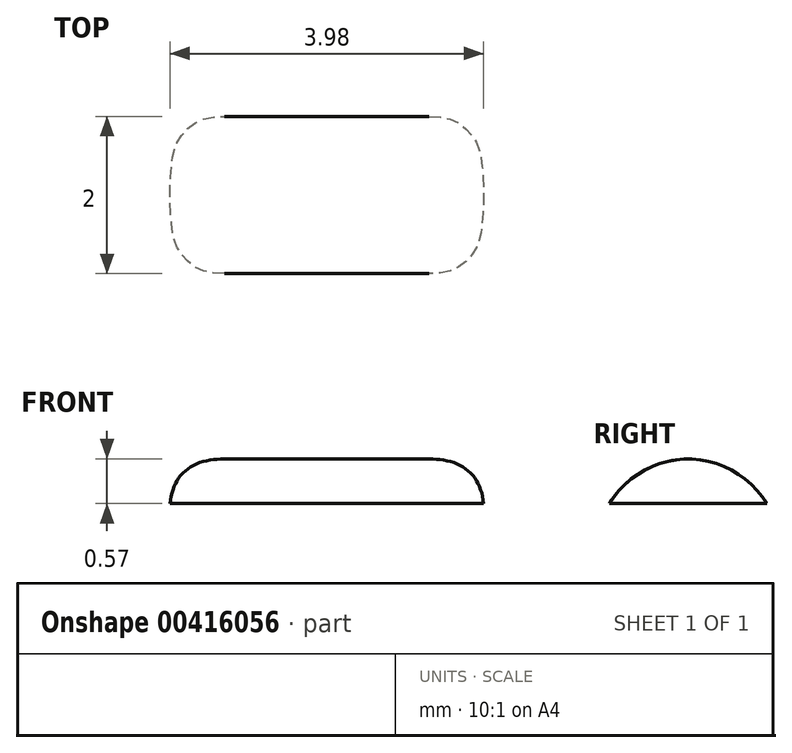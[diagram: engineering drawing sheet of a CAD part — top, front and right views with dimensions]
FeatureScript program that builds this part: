
annotation { "Feature Type Name" : "Feature", "Feature Type Description" : "" }
export const myFeature = defineFeature(function(context is Context, id is Id, definition is map)
    precondition{}
    {
        {
            var Q0;
            Q0=qCreatedBy(makeId("Right.planeOp"),FACE);
            var sketch = newSketch(context, id + "F0", { "sketchPlane" : qUnion([Q0])});
            skArc(sketch, "E0", {"start": v(1, 0) * mm, "mid": v(0, 0.57) * mm, "end": v(-1, 0) * mm});
            skLineSegment(sketch, "E1", {"start": v(-1, 0) * mm, "end": v(1, 0) * mm});
            skSolve(sketch);
        }
        {
            var Q0;
            Q0=makeQuery(id+"F0.imprint","IMPRINT",FACE,{"disambiguationData":[TD([[makeQuery(id+"F0.imprint","IMPRINT",EDGE,{"derivedFrom":sQuery(id+"F0.wireOp",EDGE,"E0")}),1.0]])]});
            extrude(context, id + "F1", {"entities" : qUnion([Q0]), "endBound" : BoundingType.SYMMETRIC, "depth" : 4 * mm});
        }
        {
            var Q0;
            Q0=makeQuery(id+"F1.opExtrude","CAP_EDGE",EDGE,{"disambiguationData":[OSD([sQuery(id+"F0.wireOp",EDGE,"E0")])],"isStart":false});
            var Q1;
            Q1=makeQuery(id+"F1.opExtrude","CAP_EDGE",EDGE,{"disambiguationData":[OSD([sQuery(id+"F0.wireOp",EDGE,"E0")])],"isStart":true});
            fillet(context, id + "F2", {"entities" : qUnion([Q0, Q1]), "radius" : 0.7 * mm, "tangentPropagation" : true, "rho" : 0.5, "crossSection" : FilletCrossSection.CONIC, "allowEdgeOverflow" : false});
        }
    });
